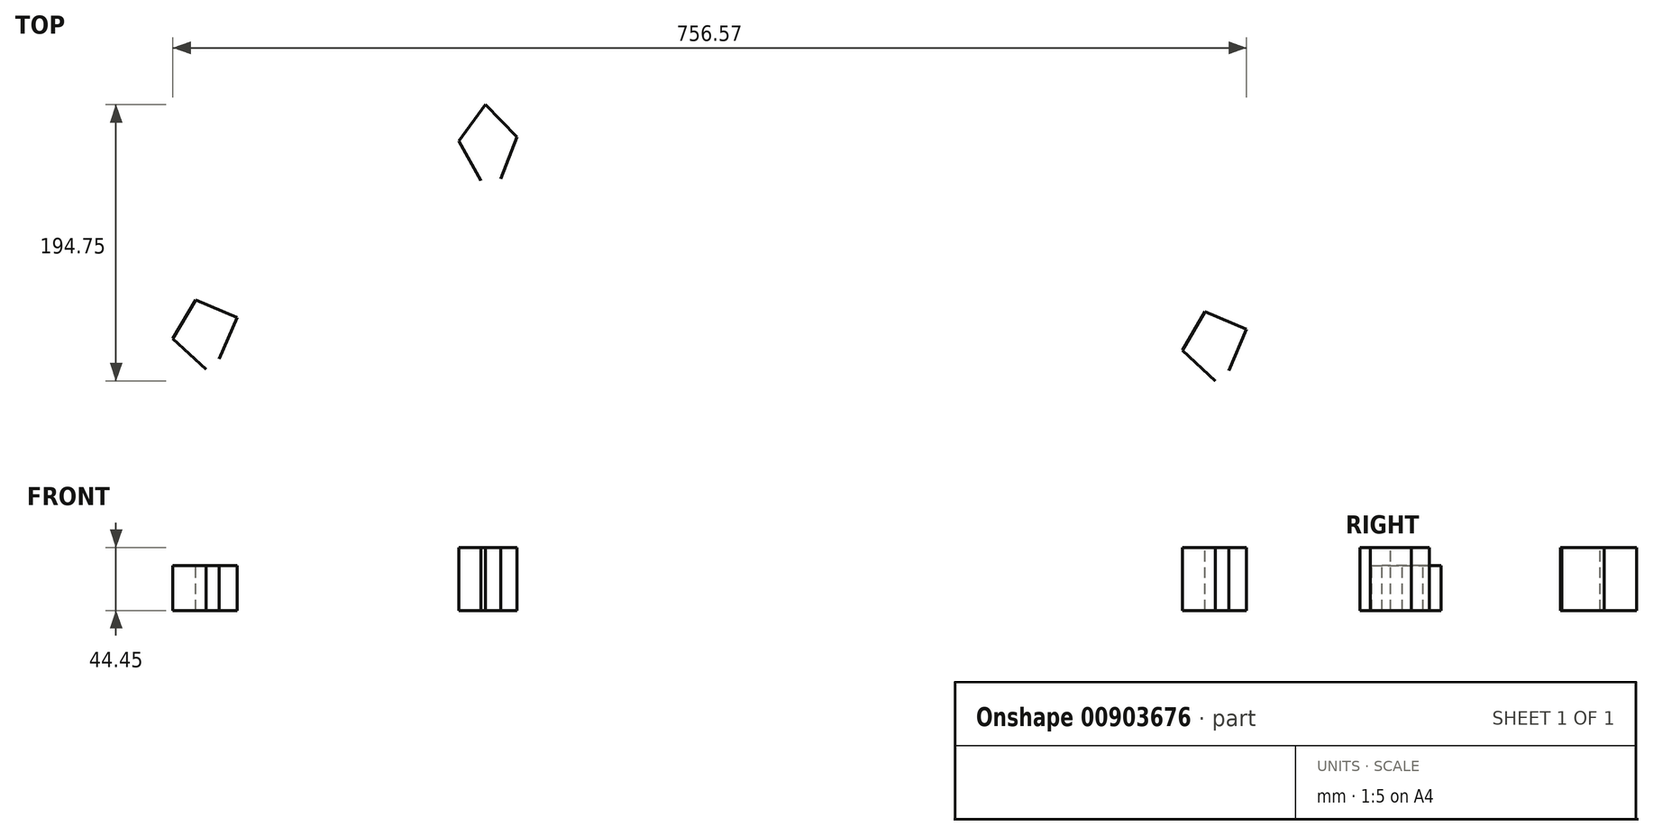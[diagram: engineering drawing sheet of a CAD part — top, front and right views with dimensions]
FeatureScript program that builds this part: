
annotation { "Feature Type Name" : "Feature", "Feature Type Description" : "" }
export const myFeature = defineFeature(function(context is Context, id is Id, definition is map)
    precondition{}
    {
        {
            var Q0;
            Q0=qCreatedBy(makeId("Top.planeOp"),FACE);
            var sketch = newSketch(context, id + "F0", { "sketchPlane" : qUnion([Q0])});
            skLineSegment(sketch, "E0", {"start": v(712.26, -35.8) * mm, "end": v(688.9, -14.28) * mm});
            skLineSegment(sketch, "E1", {"start": v(688.9, -14.28) * mm, "end": v(705.05, 13.06) * mm});
            skLineSegment(sketch, "E2", {"start": v(705.05, 13.06) * mm, "end": v(734.2, 0.46) * mm});
            skLineSegment(sketch, "E3", {"start": v(734.2, 0.46) * mm, "end": v(721.6, -28.68) * mm});
            skLineSegment(sketch, "E4", {"start": v(0.99, -27.54) * mm, "end": v(-22.37, -6.03) * mm});
            skLineSegment(sketch, "E5", {"start": v(-22.37, -6.03) * mm, "end": v(-6.22, 21.3) * mm});
            skLineSegment(sketch, "E6", {"start": v(-6.22, 21.3) * mm, "end": v(22.93, 8.71) * mm});
            skLineSegment(sketch, "E7", {"start": v(22.93, 8.71) * mm, "end": v(10.33, -20.43) * mm});
            skSolve(sketch);
        }
        {
            var Q0;
            Q0=sQuery(id+"F0.wireOp",EDGE,"E0");
            var Q1;
            Q1=sQuery(id+"F0.wireOp",EDGE,"E1");
            var Q2;
            Q2=sQuery(id+"F0.wireOp",EDGE,"E2");
            var Q3;
            Q3=sQuery(id+"F0.wireOp",EDGE,"E3");
            extrude(context, id + "F1", {"bodyType" : ToolBodyType.SURFACE, "surfaceEntities" : qUnion([Q0, Q1, Q2, Q3]), "depth" : 44.45 * mm, "offsetDistance" : 25.4 * mm});
        }
        {
            var Q0;
            Q0=qCreatedBy(makeId("Top.planeOp"),FACE);
            var sketch = newSketch(context, id + "F2", { "sketchPlane" : qUnion([Q0])});
            skLineSegment(sketch, "E8", {"start": v(0.99, -27.54) * mm, "end": v(-22.37, -6.03) * mm});
            skLineSegment(sketch, "E9", {"start": v(-22.37, -6.03) * mm, "end": v(-6.22, 21.3) * mm});
            skLineSegment(sketch, "E10", {"start": v(-6.22, 21.3) * mm, "end": v(22.93, 8.71) * mm});
            skLineSegment(sketch, "E11", {"start": v(22.93, 8.71) * mm, "end": v(10.33, -20.43) * mm});
            skSolve(sketch);
        }
        {
            var Q0;
            Q0=sQuery(id+"F2.wireOp",EDGE,"E8");
            var Q1;
            Q1=sQuery(id+"F2.wireOp",EDGE,"E11");
            var Q2;
            Q2=sQuery(id+"F2.wireOp",EDGE,"E10");
            var Q3;
            Q3=sQuery(id+"F2.wireOp",EDGE,"E9");
            extrude(context, id + "F3", {"bodyType" : ToolBodyType.SURFACE, "surfaceEntities" : qUnion([Q0, Q1, Q2, Q3]), "depth" : 31.75 * mm, "offsetDistance" : 25.4 * mm});
        }
        {
            var Q0;
            Q0=qCreatedBy(makeId("Top.planeOp"),FACE);
            var sketch = newSketch(context, id + "F4", { "sketchPlane" : qUnion([Q0])});
            skPoint(sketch, "E12.0", {"position": v(22.93, 8.71) * mm});
            skPoint(sketch, "E13.0", {"position": v(688.9, -14.28) * mm});
            skLineSegment(sketch, "E14", {"start": v(22.93, 8.71) * mm, "end": v(688.9, -14.28) * mm, "construction": true});
            skSolve(sketch);
        }
        {
            var Q0;
            Q0=qCreatedBy(makeId("Top.planeOp"),FACE);
            var sketch = newSketch(context, id + "F5", { "sketchPlane" : qUnion([Q0])});
            skLineSegment(sketch, "E15", {"start": v(194.67, 105.5) * mm, "end": v(179.28, 133.28) * mm});
            skLineSegment(sketch, "E16", {"start": v(179.28, 133.28) * mm, "end": v(197.95, 158.96) * mm});
            skLineSegment(sketch, "E17", {"start": v(197.95, 158.96) * mm, "end": v(220, 136.12) * mm});
            skLineSegment(sketch, "E18", {"start": v(220, 136.12) * mm, "end": v(208.62, 106.48) * mm});
            skSolve(sketch);
        }
        {
            var Q0;
            Q0 = qSketchRegion(id + "F5", true);
            var Q1;
            Q1 = qBodyType(qCreatedBy(id + "F5" ,EDGE), BodyType.WIRE);
            extrude(context, id + "F6", {"entities" : qUnion([Q0]), "bodyType" : ToolBodyType.SURFACE, "surfaceEntities" : qUnion([Q1]), "depth" : 44.45 * mm, "offsetDistance" : 25.4 * mm});
        }
    });
